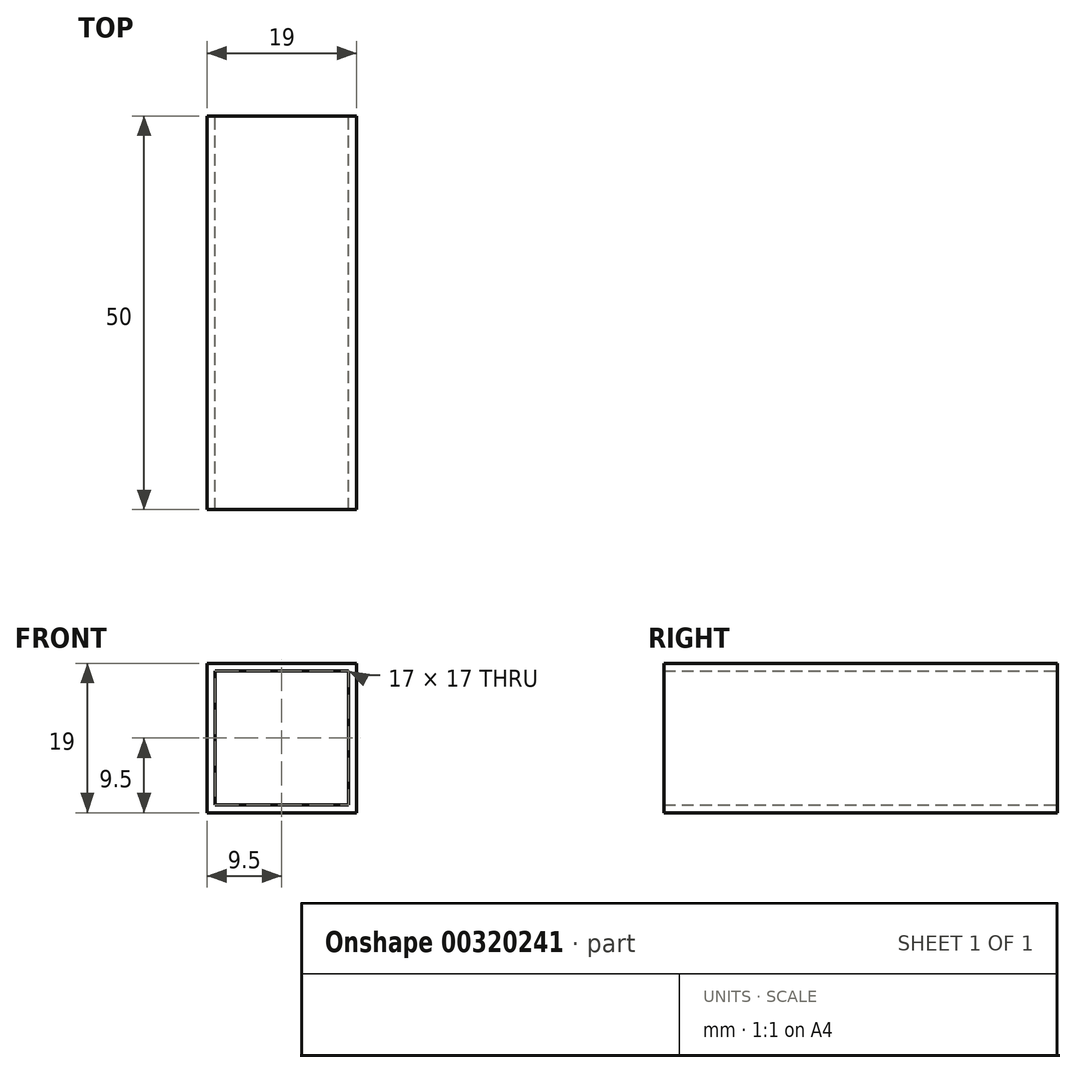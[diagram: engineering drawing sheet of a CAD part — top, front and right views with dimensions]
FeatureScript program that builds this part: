
annotation { "Feature Type Name" : "Feature", "Feature Type Description" : "" }
export const myFeature = defineFeature(function(context is Context, id is Id, definition is map)
    precondition{}
    {
        {
            var Q0;
            Q0=qCreatedBy(makeId("Front.planeOp"),FACE);
            var sketch = newSketch(context, id + "F0", { "sketchPlane" : qUnion([Q0])});
            skLineSegment(sketch, "E0.bottom", {"start": v(9.5, -9.5) * mm, "end": v(-9.5, -9.5) * mm});
            skLineSegment(sketch, "E0.top", {"start": v(9.5, 9.5) * mm, "end": v(-9.5, 9.5) * mm});
            skLineSegment(sketch, "E0.left", {"start": v(9.5, -9.5) * mm, "end": v(9.5, 9.5) * mm});
            skLineSegment(sketch, "E0.right", {"start": v(-9.5, -9.5) * mm, "end": v(-9.5, 9.5) * mm});
            skPoint(sketch, "E0.middle", {"position": v(0, 0) * mm});
            skLineSegment(sketch, "E1.0", {"start": v(8.5, 8.5) * mm, "end": v(-8.5, 8.5) * mm});
            skLineSegment(sketch, "E1.1", {"start": v(8.5, -8.5) * mm, "end": v(8.5, 8.5) * mm});
            skLineSegment(sketch, "E1.2", {"start": v(8.5, -8.5) * mm, "end": v(-8.5, -8.5) * mm});
            skLineSegment(sketch, "E1.3", {"start": v(-8.5, -8.5) * mm, "end": v(-8.5, 8.5) * mm});
            skSolve(sketch);
        }
        {
            var Q0;
            Q0 = qSketchRegion(id + "F0", true);
            extrude(context, id + "F1", {"entities" : qUnion([Q0]), "depth" : 50 * mm});
        }
    });
